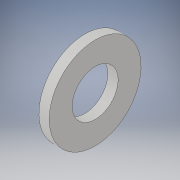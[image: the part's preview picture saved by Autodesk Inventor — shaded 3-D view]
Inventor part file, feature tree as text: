
AUTODESK INVENTOR PART (.ipt)
format: ipt  version: 2018 (Build 220112000, 112)  size: 98,816 bytes
history: native  units: in
note: dims shown in document units (in); Inventor stores cm internally (conversion verified against a paired STEP export)
features: extrude x1, sketch x1
ambient origin geometry x8: Origin, YZ Plane, XZ Plane, XY Plane, X Axis, Y Axis, Z Axis, Center Point
bodies: Solid1 (feature_tree)
feature tree (2):
  extrude  "Extrusion1"  Depth=0.2188in
  sketch  "Sketch1"  dims[d0=0.4375in d1=0.2188in d2=0.049in d3=0.0in]
